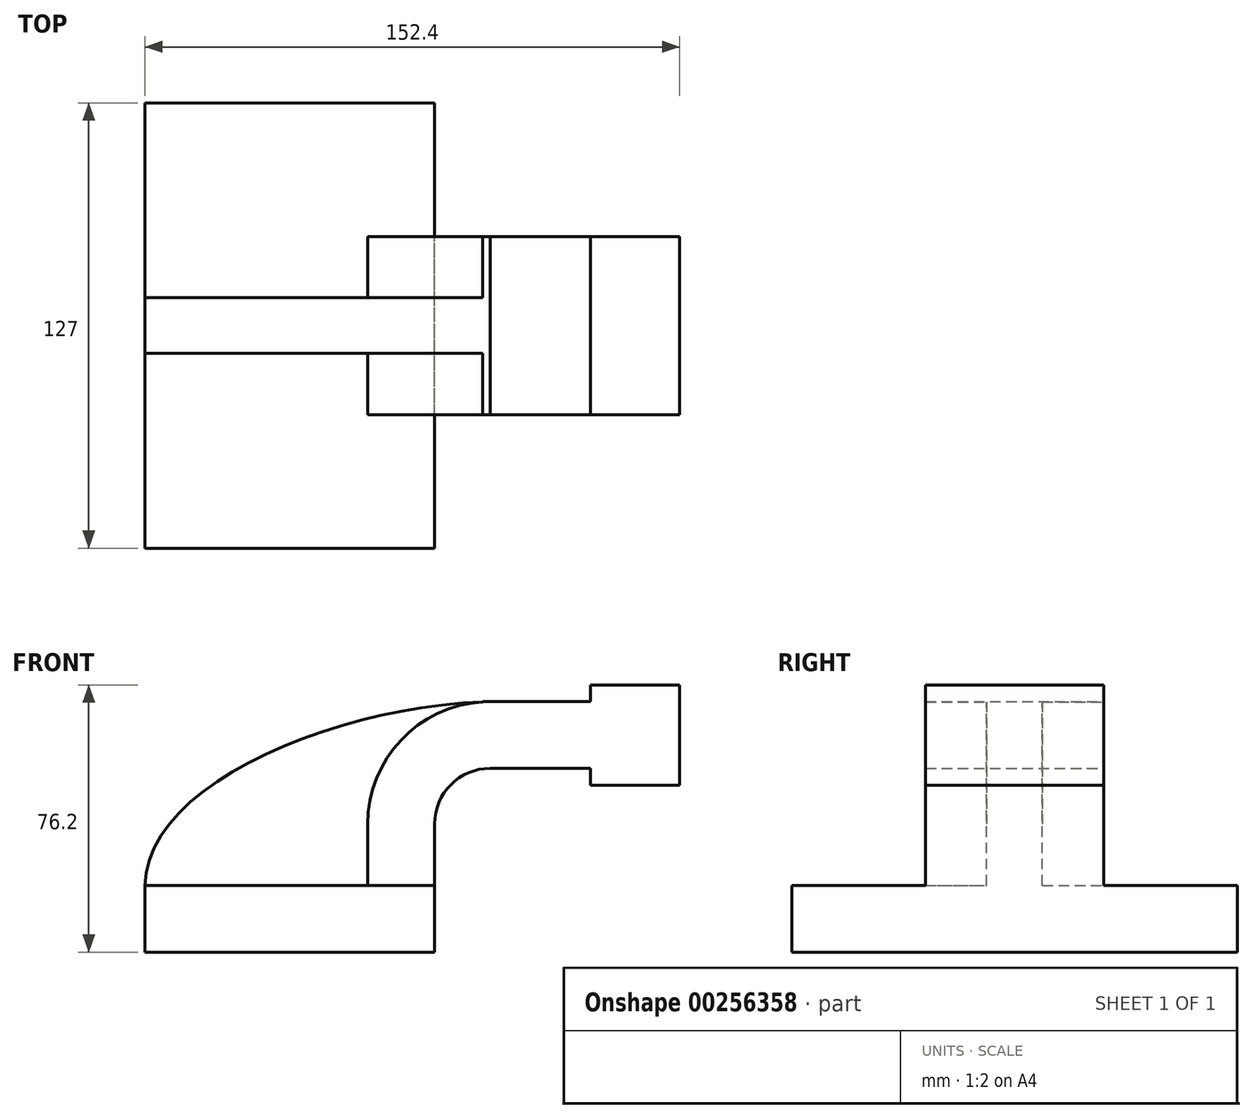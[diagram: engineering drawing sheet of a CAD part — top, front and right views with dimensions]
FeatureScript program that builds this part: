
annotation { "Feature Type Name" : "Feature", "Feature Type Description" : "" }
export const myFeature = defineFeature(function(context is Context, id is Id, definition is map)
    precondition{}
    {
        {
            var Q0;
            Q0=qCreatedBy(makeId("Front.planeOp"),FACE);
            var sketch = newSketch(context, id + "F0", { "sketchPlane" : qUnion([Q0])});
            skLineSegment(sketch, "E0.bottom", {"start": v(-41.28, -9.53) * mm, "end": v(41.28, -9.53) * mm});
            skLineSegment(sketch, "E0.top", {"start": v(-41.28, 9.53) * mm, "end": v(41.28, 9.53) * mm});
            skLineSegment(sketch, "E0.left", {"start": v(-41.28, -9.53) * mm, "end": v(-41.28, 9.53) * mm});
            skLineSegment(sketch, "E0.right", {"start": v(41.28, -9.53) * mm, "end": v(41.28, 9.52) * mm});
            skPoint(sketch, "E0.middle", {"position": v(0, 0) * mm});
            skLineSegment(sketch, "E1.bottom", {"start": v(111.12, 38.1) * mm, "end": v(60.32, 38.1) * mm});
            skLineSegment(sketch, "E1.top", {"start": v(111.12, 66.67) * mm, "end": v(60.32, 66.67) * mm});
            skLineSegment(sketch, "E1.left", {"start": v(111.12, 38.1) * mm, "end": v(111.12, 66.67) * mm});
            skLineSegment(sketch, "E1.right", {"start": v(60.32, 38.1) * mm, "end": v(60.32, 66.67) * mm});
            skPoint(sketch, "E1.middle", {"position": v(85.72, 52.39) * mm});
            skLineSegment(sketch, "E2", {"start": v(41.28, 9.52) * mm, "end": v(41.28, 27) * mm});
            skArc(sketch, "E3", {"start": v(41.27, 27) * mm, "mid": v(45.92, 38.23) * mm, "end": v(57.15, 42.88) * mm});
            skLineSegment(sketch, "E4", {"start": v(57.15, 42.88) * mm, "end": v(85.72, 42.88) * mm});
            skPoint(sketch, "E4.endSnap0", {"position": v(85.72, 38.1) * mm});
            skLineSegment(sketch, "E5.0", {"start": v(57.15, 61.93) * mm, "end": v(85.72, 61.93) * mm});
            skArc(sketch, "E5.1", {"start": v(22.23, 27) * mm, "mid": v(32.45, 51.7) * mm, "end": v(57.15, 61.93) * mm});
            skLineSegment(sketch, "E5.2", {"start": v(22.23, 9.52) * mm, "end": v(22.23, 27) * mm});
            skLineSegment(sketch, "E6", {"start": v(85.72, 38.1) * mm, "end": v(85.72, 66.67) * mm});
            skFitSpline(sketch, "E7", {"points": [v(-41.28, 9.53) * mm, v(57.15, 61.93) * mm], "startDerivative": vector(0.6, 86.4) * mm, "endDerivative": vector(131.54, 3.12) * mm});
            skSolve(sketch);
        }
        {
            var Q0;
            Q0=makeQuery(id+"F0.imprint","IMPRINT",FACE,{"disambiguationData":[TD([[makeQuery(id+"F0.imprint","IMPRINT",EDGE,{"derivedFrom":sQuery(id+"F0.wireOp",EDGE,"E0.bottom")}),1.0]])]});
            extrude(context, id + "F1", {"entities" : qUnion([Q0]), "endBound" : BoundingType.SYMMETRIC, "depth" : 127 * mm});
        }
        {
            var Q0;
            {var subQ1=sQuery(id+"F0.wireOp",EDGE,"E2");Q0=makeQuery(id+"F0.imprint","IMPRINT",FACE,{"disambiguationData":[TD([[makeQuery(id+"F0.imprint","IMPRINT",EDGE,{"derivedFrom":subQ1}),1.0]])]});}
            var Q1;
            {var subQ0=sQuery(id+"F0.wireOp",EDGE,"E4");var subQ1=sQuery(id+"F0.wireOp",EDGE,"E1.right");var subQ2=makeQuery(id+"F0.imprint","INTERSECT",VERTEX,{"derivedFrom":[subQ1,subQ0]});Q1=makeQuery(id+"F0.imprint","IMPRINT",FACE,{"disambiguationData":[TD([[makeQuery(id+"F0.imprint","IMPRINT",EDGE,{"disambiguationData":[TD([[subQ2,-1.0]])],"derivedFrom":subQ1}),-1.0]])]});}
            var Q2;
            {var subQ0=sQuery(id+"F0.wireOp",EDGE,"E1.left");Q2=makeQuery(id+"F0.imprint","IMPRINT",FACE,{"disambiguationData":[TD([[makeQuery(id+"F0.imprint","IMPRINT",EDGE,{"derivedFrom":subQ0}),1.0]])]});}
            extrude(context, id + "F2", {"entities" : qUnion([Q0, Q1, Q2]), "operationType" : NewBodyOperationType.ADD, "endBound" : BoundingType.SYMMETRIC, "depth" : 50.8 * mm});
        }
        {
            var Q0;
            {var subQ3=sQuery(id+"F0.wireOp",EDGE,"E5.2");Q0=makeQuery(id+"F0.imprint","IMPRINT",FACE,{"disambiguationData":[TD([[makeQuery(id+"F0.imprint","IMPRINT",EDGE,{"derivedFrom":subQ3}),1.0]])]});}
            extrude(context, id + "F3", {"entities" : qUnion([Q0]), "operationType" : NewBodyOperationType.ADD, "endBound" : BoundingType.SYMMETRIC, "depth" : 15.88 * mm});
        }
    });
